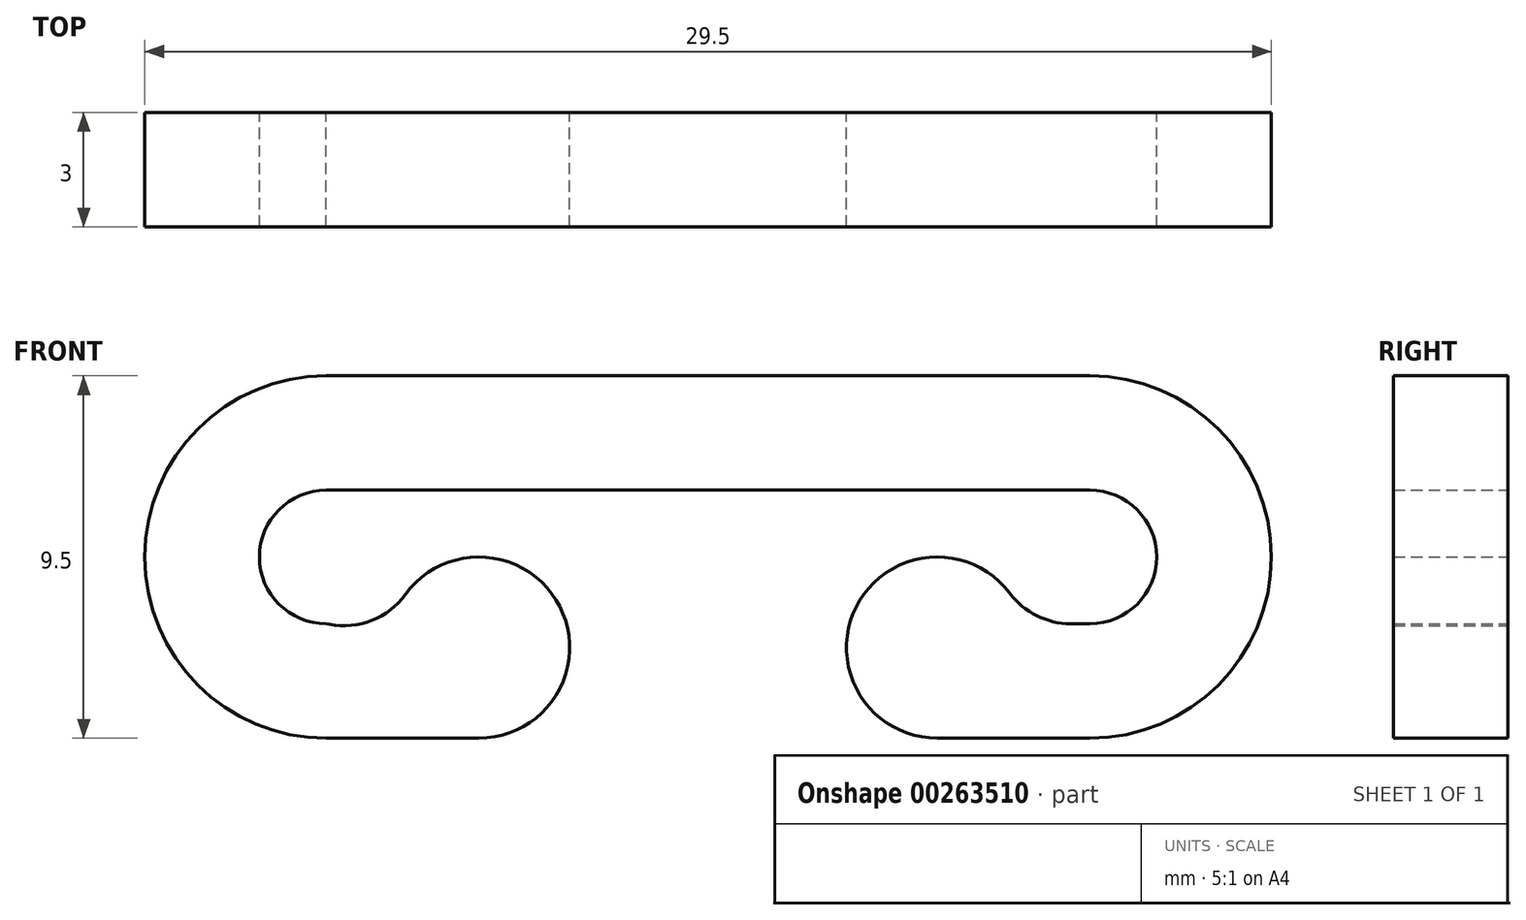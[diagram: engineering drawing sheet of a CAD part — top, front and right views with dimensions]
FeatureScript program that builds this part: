
annotation { "Feature Type Name" : "Feature", "Feature Type Description" : "" }
export const myFeature = defineFeature(function(context is Context, id is Id, definition is map)
    precondition{}
    {
        {
            var Q0;
            Q0=qCreatedBy(makeId("Front.planeOp"),FACE);
            var sketch = newSketch(context, id + "F0", { "sketchPlane" : qUnion([Q0])});
            skArc(sketch, "E0", {"start": v(0, -1.75) * mm, "mid": v(1.75, 0) * mm, "end": v(0, 1.75) * mm});
            skArc(sketch, "E1", {"start": v(-20, 1.75) * mm, "mid": v(-21.75, 0) * mm, "end": v(-20, -1.75) * mm});
            skArc(sketch, "E2", {"start": v(-20, 4.75) * mm, "mid": v(-24.75, 0) * mm, "end": v(-20, -4.75) * mm});
            skLineSegment(sketch, "E3", {"start": v(0, 4.75) * mm, "end": v(-20, 4.75) * mm});
            skLineSegment(sketch, "E4", {"start": v(0, 1.75) * mm, "end": v(-20, 1.75) * mm});
            skLineSegment(sketch, "E5", {"start": v(0, -1.75) * mm, "end": v(-0.5, -1.75) * mm});
            skLineSegment(sketch, "E6", {"start": v(0, -4.75) * mm, "end": v(-4, -4.75) * mm});
            skArc(sketch, "E7", {"start": v(-2.1, -0.95) * mm, "mid": v(-6.12, -1.31) * mm, "end": v(-4, -4.75) * mm});
            skArc(sketch, "E8", {"start": v(-16, -4.75) * mm, "mid": v(-13.88, -1.3) * mm, "end": v(-17.92, -0.98) * mm});
            skPoint(sketch, "E9.orphan", {"position": v(-16, 0) * mm});
            skArc(sketch, "E10.trimOffspring", {"start": v(0, -4.75) * mm, "mid": v(4.75, 0) * mm, "end": v(0, 4.75) * mm});
            skPoint(sketch, "E11.orphan", {"position": v(-4, -4.75) * mm});
            skPoint(sketch, "E12.start.orphan", {"position": v(-4, 0) * mm});
            skPoint(sketch, "E13.orphan", {"position": v(-16, -4.75) * mm});
            skLineSegment(sketch, "E14.trimOffspring", {"start": v(-19.92, -1.77) * mm, "end": v(-20, -1.75) * mm});
            skLineSegment(sketch, "E15.trimOffspring", {"start": v(-16, -4.75) * mm, "end": v(-20, -4.75) * mm});
            skPoint(sketch, "E16.visualSharp", {"position": v(-18.36, -2.07) * mm});
            skArc(sketch, "E16.filletArc", {"start": v(-19.92, -1.77) * mm, "mid": v(-18.8, -1.66) * mm, "end": v(-17.92, -0.98) * mm});
            skPoint(sketch, "E17.visualSharp", {"position": v(-1.7, -1.75) * mm});
            skArc(sketch, "E17.filletArc", {"start": v(-2.1, -0.95) * mm, "mid": v(-1.4, -1.54) * mm, "end": v(-0.5, -1.75) * mm});
            skSolve(sketch);
        }
        {
            var Q0;
            Q0 = qSketchRegion(id + "F0", true);
            extrude(context, id + "F1", {"entities" : qUnion([Q0]), "depth" : 3 * mm});
        }
    });
